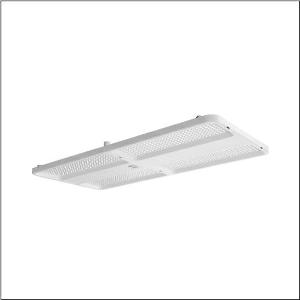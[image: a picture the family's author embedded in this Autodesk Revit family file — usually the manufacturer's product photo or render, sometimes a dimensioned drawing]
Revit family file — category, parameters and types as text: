
# Revit family: highbay_21_maxi_52hn12db4qda03
name_source: partatom
category: Lighting Fixtures
units: mm (PartAtom-declared; Revit-internal decimal feet)

## family parameters
Cut with Voids When Loaded = No
Host = Face
Light Source = No
Part Type = Normal
Room Calculation Point = No
Round Connector Dimension = Use Diameter
Shared = No

## types (1)
- --- (1 x LED, 38000 lm, 197.7 W, 4000K)
    Apparent Load = 198 VA
    CIE Flux Codes = 90 98 100 100 100
    Color Rendering = 80
    Color Temperature = 4000K
    Default Elevation = 1800 mm
    Description = high bay luminaire Highbay 21 maxi; direct symmetric wide distribution, light control with lens of PMMA; UGR ≤ 22 (X = 4H | Y = 8H | S = 0.25H | reflection values 70/50/20); luminous flux: 38.000lm; light colour: 840, colour temperature: 4000K, MacAdam ≤ 3 SDCM (initial), colour rendering: CRI > 80; luminous efficacy: 192,2lm/W; rated service life: 75.000h (L80) at AT= ta max; control: DALI 2; for wired networking: open and standardized DALI2 interface enables full flexibility and future-proofing for changes in use or functional adaptation through individual programming; multi-sensor luminaire consisting of a DALI2 multi-sensor and DALI2 ECG; multi-sensor luminaire for wired connection to a DALI2 application controller (e.g., SITECO Connect 11 or 21); can also be connected to existing on-site lighting or building automation systems upon request; integrated DALI2 sensor certified according to IEC 62386, Parts 101, 103, 303, and 304; integrated DALI2 ECG provides luminaire data (according to IEC 62386, Part 251), energy data (Part 252), and monitoring and analytics data (Part 253) to higher-level systems for further processing; luminaire with PIR sensor (passive-infrared); with light sensor; luminaire connection: terminal, 5-pole, max. 2.5mm² (cable entry for one cable, Ø 8.5..16mm); mains connection: 230..240V, AC 50/60Hz; connected load: 197,7W; protection rating (complete): IP65; insulation class (complete): insulation class I (protective earthing); protection symbol: D; certification: CE, UKCA; internal wiring halogen-free; luminaire LABS conformity tested according to VDMA 24364:2018-05; Suitable for use in the food industry according to the specifications of IFS-Food, HACCP and/or BRC; housing frame of high-performance plastic PA6, matt traffic white (RAL 9016); cover of PMMA; dimension (LxWxH): 946 x 442 x 72mm; permissible operating ambient temperature: -20..+40°C (reducing of maximum allowable ambient temperature of 5°C with ceiling mounting); packaging unit: 1 piece; (delivery without accessories; please order mounting accessories separately)
    Height = 72 mm  [stored 0.23622 ft]
    Lamp = 1 x LED
    Lamp Light Flux = 38000 lm
    Lamp Power = 197.7 W
    Lamp count = 1
    Length = 946 mm
    Luminous efficacy = 192 lm/W
    Manufacturer = Siteco
    ModVariant = No
    Model = 52HN12DB4QDA03
    Mounting Place = Ceiling
    Mounting Type = Pendant
    Number of Poles = 1
    OnlyDefault = Yes
    Power Factor = 1
    Product Name = Highbay 21 maxi
    Product group = high bay luminaire
    ProductGroupID = 902
    Protection Class = Protection class I
    Protection Degree = IP 65
    RLX_Detail_Level = 1
    RLX_Emergency_Light_Flux = 0 lm
    RLX_Emergency_Type = 0
    RLX_Emergency_Type_DB = No
    RlxData = <blob elided: 128469 chars, md5=76b33fb1>
    Socket = socket
    Standby Power = 0 W
    System Light Flux = 38000 lm
    System Power = 198 W
    Type Comments = factory setting: luminous flux: 100 % | dim-lin: 254 | 918 mA
    Type Image = l_1363267.jpg
    URL = http://relux.com
    VarID = @adj_013751
    Voltage = 0 V
    Weight = 0.00 kg
    Width = 442 mm

note: [stored X ft] marks values corroborated as IEEE doubles in the binary element streams (Revit-internal decimal feet)

## geometry (parser evidence)
native form markers: Blend x4, Sweep x10
no freeform markers — native parametric forms only
